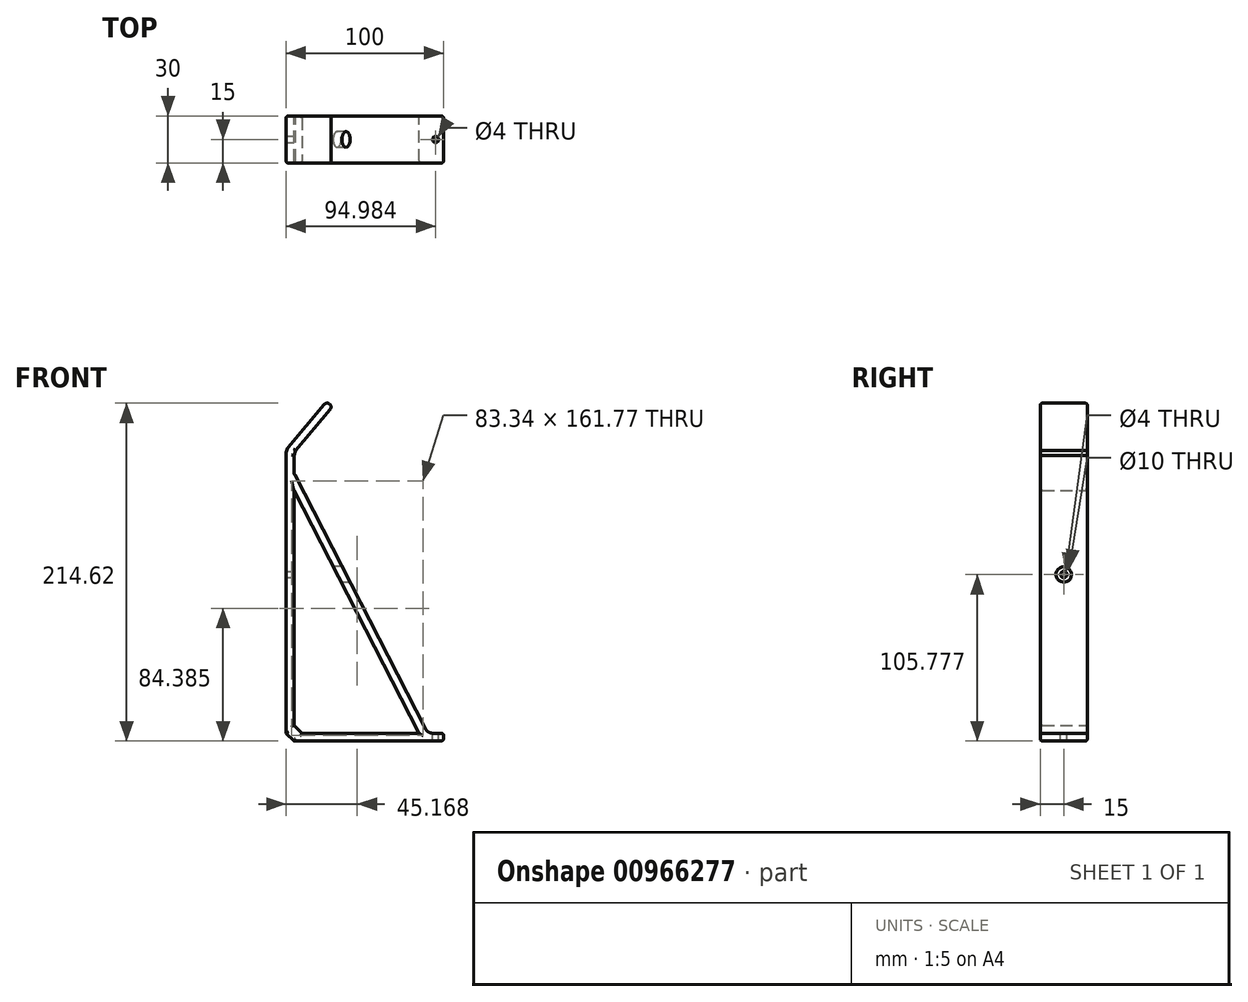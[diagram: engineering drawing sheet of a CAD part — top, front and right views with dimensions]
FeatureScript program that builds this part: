
annotation { "Feature Type Name" : "Feature", "Feature Type Description" : "" }
export const myFeature = defineFeature(function(context is Context, id is Id, definition is map)
    precondition{}
    {
        {
            var Q0;
            Q0=qCreatedBy(makeId("Front.planeOp"),FACE);
            var sketch = newSketch(context, id + "F0", { "sketchPlane" : qUnion([Q0])});
            skLineSegment(sketch, "E0", {"start": v(10, 0) * mm, "end": v(90, 0) * mm});
            skLineSegment(sketch, "E1", {"start": v(90, 0) * mm, "end": v(90, 5) * mm});
            skLineSegment(sketch, "E2", {"start": v(90, 5) * mm, "end": v(5, 5) * mm});
            skLineSegment(sketch, "E3", {"start": v(5, 5) * mm, "end": v(5, 170) * mm});
            skLineSegment(sketch, "E4", {"start": v(5, 183.18) * mm, "end": v(29.54, 212.43) * mm});
            skLineSegment(sketch, "E5", {"start": v(29.54, 212.43) * mm, "end": v(25.71, 215.64) * mm});
            skLineSegment(sketch, "E6", {"start": v(25.71, 215.64) * mm, "end": v(0, 185) * mm});
            skLineSegment(sketch, "E7", {"start": v(0, 185) * mm, "end": v(0, 5) * mm});
            skLineSegment(sketch, "E8", {"start": v(5, 170) * mm, "end": v(5, 183.18) * mm});
            skLineSegment(sketch, "E9", {"start": v(5, 170) * mm, "end": v(90, 5) * mm});
            skLineSegment(sketch, "E10", {"start": v(5, 159.08) * mm, "end": v(84.38, 5) * mm});
            skLineSegment(sketch, "E11", {"start": v(53.13, 76.58) * mm, "end": v(48.68, 74.3) * mm, "construction": true});
            skPoint(sketch, "E12.visualSharp", {"position": v(0, 0) * mm});
            skLineSegment(sketch, "E13", {"start": v(5, 5) * mm, "end": v(5, 5) * mm});
            skLineSegment(sketch, "E14", {"start": v(0, 5) * mm, "end": v(0, 0) * mm});
            skLineSegment(sketch, "E15", {"start": v(10, 0) * mm, "end": v(0, 0) * mm});
            skLineSegment(sketch, "E16", {"start": v(5, 5) * mm, "end": v(0, 5) * mm, "construction": true});
            skLineSegment(sketch, "E17.bottom", {"start": v(90, 5) * mm, "end": v(100, 5) * mm});
            skLineSegment(sketch, "E17.top", {"start": v(90, 0) * mm, "end": v(100, 0) * mm});
            skLineSegment(sketch, "E17.left", {"start": v(90, 5) * mm, "end": v(90, 0) * mm});
            skLineSegment(sketch, "E17.right", {"start": v(100, 5) * mm, "end": v(100, 0) * mm});
            skSolve(sketch);
        }
        {
            var Q0;
            Q0=makeQuery(id+"F0.imprint","IMPRINT",FACE,{"disambiguationData":[TD([[makeQuery(id+"F0.imprint","IMPRINT",EDGE,{"derivedFrom":sQuery(id+"F0.wireOp",EDGE,"E0")}),1.0]])]});
            var Q1;
            Q1=makeQuery(id+"F0.imprint","IMPRINT",FACE,{"disambiguationData":[TD([[makeQuery(id+"F0.imprint","IMPRINT",EDGE,{"derivedFrom":sQuery(id+"F0.wireOp",EDGE,"E4")}),1.0]])]});
            var Q2;
            {var subQ0=sQuery(id+"F0.wireOp",EDGE,"E9");Q2=makeQuery(id+"F0.imprint","IMPRINT",FACE,{"disambiguationData":[TD([[makeQuery(id+"F0.imprint","IMPRINT",EDGE,{"derivedFrom":subQ0}),-1.0]])]});}
            var Q3;
            Q3=makeQuery(id+"F0.imprint","IMPRINT",FACE,{"disambiguationData":[TD([[makeQuery(id+"F0.imprint","IMPRINT",EDGE,{"derivedFrom":sQuery(id+"F0.wireOp",EDGE,"E14")}),1.0]])]});
            var Q4;
            Q4=makeQuery(id+"F0.imprint","IMPRINT",FACE,{"disambiguationData":[TD([[makeQuery(id+"F0.imprint","IMPRINT",EDGE,{"derivedFrom":sQuery(id+"F0.wireOp",EDGE,"E17.bottom")}),-1.0]])]});
            extrude(context, id + "F1", {"entities" : qUnion([Q0, Q1, Q2, Q3, Q4]), "depth" : 30 * mm, "offsetDistance" : 25 * mm});
        }
        {
            var Q0;
            Q0=makeQuery(id+"F1.opExtrude","SWEPT_EDGE",EDGE,{"disambiguationData":[OSD([sQuery(id+"F0.wireOp",EDGE,"E0"),sQuery(id+"F0.wireOp",EDGE,"E1")])]});
            var Q1;
            Q1=makeQuery(id+"F1.opExtrude","SWEPT_EDGE",EDGE,{"disambiguationData":[OSD([sQuery(id+"F0.wireOp",EDGE,"E3"),sQuery(id+"F0.wireOp",EDGE,"E8"),sQuery(id+"F0.wireOp",EDGE,"E9")])]});
            fillet(context, id + "F2", {"entities" : qUnion([Q0, Q1]), "radius" : 5 * mm, "tangentPropagation" : true, "allowEdgeOverflow" : false});
        }
        {
            var Q0;
            Q0=makeQuery(id+"F1.opExtrude","SWEPT_EDGE",EDGE,{"disambiguationData":[OSD([sQuery(id+"F0.wireOp",EDGE,"E5"),sQuery(id+"F0.wireOp",EDGE,"E6")])]});
            var Q1;
            Q1=makeQuery(id+"F1.opExtrude","SWEPT_EDGE",EDGE,{"disambiguationData":[OSD([sQuery(id+"F0.wireOp",EDGE,"E4"),sQuery(id+"F0.wireOp",EDGE,"E5")])]});
            fillet(context, id + "F3", {"entities" : qUnion([Q0, Q1]), "radius" : 2.5 * mm, "tangentPropagation" : true, "allowEdgeOverflow" : false});
        }
        {
            var Q0;
            Q0=makeQuery(id+"F1.opExtrude","SWEPT_FACE",FACE,{"disambiguationData":[OSD([sQuery(id+"F0.wireOp",EDGE,"E3")])]});
            var sketch = newSketch(context, id + "F4", { "sketchPlane" : qUnion([Q0])});
            skCircle(sketch, "E18", {"center": v(-15, 105.78) * mm, "radius": 2 * mm});
            skCircle(sketch, "E19.0", {"center": v(-15, 105.78) * mm, "radius": 5 * mm});
            skLineSegment(sketch, "E20", {"start": v(-15, 105.78) * mm, "end": v(-30, 105.78) * mm, "construction": true});
            skLineSegment(sketch, "E21", {"start": v(-15, 105.78) * mm, "end": v(0, 105.78) * mm, "construction": true});
            skSolve(sketch);
        }
        {
            var Q0;
            Q0=makeQuery(id+"F4.imprint","IMPRINT",FACE,{"disambiguationData":[TD([[makeQuery(id+"F4.imprint","IMPRINT",EDGE,{"derivedFrom":sQuery(id+"F4.wireOp",EDGE,"E18")}),1.0]])]});
            extrude(context, id + "F5", {"entities" : qUnion([Q0]), "operationType" : NewBodyOperationType.REMOVE, "oppositeDirection" : true, "depth" : 25 * mm, "offsetDistance" : 25 * mm});
        }
        {
            var Q0;
            Q0=makeQuery(id+"F4.imprint","IMPRINT",FACE,{"disambiguationData":[TD([[makeQuery(id+"F4.imprint","IMPRINT",EDGE,{"derivedFrom":sQuery(id+"F4.wireOp",EDGE,"E18")}),-1.0]])]});
            var Q1;
            Q1=makeQuery(id+"F4.imprint","IMPRINT",FACE,{"disambiguationData":[TD([[makeQuery(id+"F4.imprint","IMPRINT",EDGE,{"derivedFrom":sQuery(id+"F4.wireOp",EDGE,"E18")}),1.0]])]});
            extrude(context, id + "F6", {"entities" : qUnion([Q0, Q1]), "operationType" : NewBodyOperationType.REMOVE, "depth" : 40 * mm, "offsetDistance" : 25 * mm});
        }
        {
            var Q0;
            Q0=makeQuery(id+"F1.opExtrude","SWEPT_FACE",FACE,{"disambiguationData":[OSD([sQuery(id+"F0.wireOp",EDGE,"E2")])]});
            var sketch = newSketch(context, id + "F7", { "sketchPlane" : qUnion([Q0])});
            skCircle(sketch, "E22", {"center": v(94.98, -15) * mm, "radius": 2 * mm});
            skCircle(sketch, "E23.0", {"center": v(94.98, -15) * mm, "radius": 5 * mm});
            skLineSegment(sketch, "E24", {"start": v(94.98, -15) * mm, "end": v(94.98, -30) * mm, "construction": true});
            skLineSegment(sketch, "E25", {"start": v(94.98, -15) * mm, "end": v(94.98, 0) * mm, "construction": true});
            skSolve(sketch);
        }
        {
            var Q0;
            Q0=makeQuery(id+"F7.imprint","IMPRINT",FACE,{"disambiguationData":[TD([[makeQuery(id+"F7.imprint","IMPRINT",EDGE,{"derivedFrom":sQuery(id+"F7.wireOp",EDGE,"E22")}),1.0]])]});
            extrude(context, id + "F8", {"entities" : qUnion([Q0]), "operationType" : NewBodyOperationType.REMOVE, "oppositeDirection" : true, "depth" : 25 * mm, "offsetDistance" : 25 * mm});
        }
        {
            var Q0;
            Q0=makeQuery(id+"F1.opExtrude","SWEPT_EDGE",EDGE,{"disambiguationData":[OSD([sQuery(id+"F0.wireOp",EDGE,"E2"),sQuery(id+"F0.wireOp",EDGE,"E3")])]});
            var Q1;
            Q1=makeQuery(id+"F1.opExtrude","SWEPT_EDGE",EDGE,{"disambiguationData":[OSD([sQuery(id+"F0.wireOp",EDGE,"E14"),sQuery(id+"F0.wireOp",EDGE,"E15")])]});
            var Q2;
            Q2=makeQuery(id+"F1.opExtrude","SWEPT_EDGE",EDGE,{"disambiguationData":[OSD([sQuery(id+"F0.wireOp",EDGE,"E6"),sQuery(id+"F0.wireOp",EDGE,"E7")])]});
            var Q3;
            Q3=makeQuery(id+"F1.opExtrude","SWEPT_EDGE",EDGE,{"disambiguationData":[OSD([sQuery(id+"F0.wireOp",EDGE,"E4"),sQuery(id+"F0.wireOp",EDGE,"E8")])]});
            chamfer(context, id + "F9", {"entities" : qUnion([Q0, Q1, Q2, Q3]), "width" : 5 * mm, "tangentPropagation" : true});
        }
        {
            var Q0;
            Q0=makeQuery(id+"F1.opExtrude","SWEPT_EDGE",EDGE,{"disambiguationData":[OSD([sQuery(id+"F0.wireOp",EDGE,"E17.bottom"),sQuery(id+"F0.wireOp",EDGE,"E17.right")])]});
            var Q1;
            Q1=makeQuery(id+"F1.opExtrude","CAP_FACE",FACE,{"disambiguationData":[OSD([sQuery(id+"F0.wireOp",EDGE,"E0"),sQuery(id+"F0.wireOp",EDGE,"E2"),sQuery(id+"F0.wireOp",EDGE,"E3"),sQuery(id+"F0.wireOp",EDGE,"E4"),sQuery(id+"F0.wireOp",EDGE,"E5"),sQuery(id+"F0.wireOp",EDGE,"E6"),sQuery(id+"F0.wireOp",EDGE,"E7"),sQuery(id+"F0.wireOp",EDGE,"E8"),sQuery(id+"F0.wireOp",EDGE,"E9"),sQuery(id+"F0.wireOp",EDGE,"E10"),sQuery(id+"F0.wireOp",EDGE,"E14"),sQuery(id+"F0.wireOp",EDGE,"E15"),sQuery(id+"F0.wireOp",EDGE,"E17.bottom"),sQuery(id+"F0.wireOp",EDGE,"E17.top"),sQuery(id+"F0.wireOp",EDGE,"E17.right")])],"isStart":false});
            var Q2;
            Q2=makeQuery(id+"F1.opExtrude","CAP_FACE",FACE,{"disambiguationData":[OSD([sQuery(id+"F0.wireOp",EDGE,"E0"),sQuery(id+"F0.wireOp",EDGE,"E2"),sQuery(id+"F0.wireOp",EDGE,"E3"),sQuery(id+"F0.wireOp",EDGE,"E4"),sQuery(id+"F0.wireOp",EDGE,"E5"),sQuery(id+"F0.wireOp",EDGE,"E6"),sQuery(id+"F0.wireOp",EDGE,"E7"),sQuery(id+"F0.wireOp",EDGE,"E8"),sQuery(id+"F0.wireOp",EDGE,"E9"),sQuery(id+"F0.wireOp",EDGE,"E10"),sQuery(id+"F0.wireOp",EDGE,"E14"),sQuery(id+"F0.wireOp",EDGE,"E15"),sQuery(id+"F0.wireOp",EDGE,"E17.bottom"),sQuery(id+"F0.wireOp",EDGE,"E17.top"),sQuery(id+"F0.wireOp",EDGE,"E17.right")])],"isStart":true});
            var Q3;
            Q3=makeQuery(id+"F1.opExtrude","SWEPT_EDGE",EDGE,{"disambiguationData":[OSD([sQuery(id+"F0.wireOp",EDGE,"E17.top"),sQuery(id+"F0.wireOp",EDGE,"E17.right")])]});
            var Q4;
            Q4=makeQuery(id+"F5.boolean.opBoolean","COPY",EDGE,{"derivedFrom":makeQuery(id+"F5.opExtrude","CAP_EDGE",EDGE,{"disambiguationData":[OSD([sQuery(id+"F4.wireOp",EDGE,"E18")])],"isStart":true})});
            var Q5;
            Q5=makeQuery(id+"F8.boolean.opBoolean","COPY",EDGE,{"derivedFrom":makeQuery(id+"F8.opExtrude","CAP_EDGE",EDGE,{"disambiguationData":[OSD([sQuery(id+"F7.wireOp",EDGE,"E22")])],"isStart":true})});
            var Q6;
            {var subQ0=sQuery(id+"F0.wireOp",EDGE,"E6");Q6=makeQuery(id+"F9.opChamfer","BLEND_EDGE",EDGE,{"blendedFrom":[makeQuery(id+"F1.opExtrude","SWEPT_EDGE",EDGE,{"disambiguationData":[OSD([subQ0,sQuery(id+"F0.wireOp",EDGE,"E7")])]}),makeQuery(id+"F1.opExtrude","SWEPT_FACE",FACE,{"disambiguationData":[OSD([subQ0])]})],"blendedInto":[makeQuery(id+"F1.opExtrude","SWEPT_FACE",FACE,{"disambiguationData":[OSD([subQ0])]})]});}
            var Q7;
            {var subQ0=sQuery(id+"F0.wireOp",EDGE,"E7");Q7=makeQuery(id+"F9.opChamfer","BLEND_EDGE",EDGE,{"blendedFrom":[makeQuery(id+"F1.opExtrude","SWEPT_EDGE",EDGE,{"disambiguationData":[OSD([sQuery(id+"F0.wireOp",EDGE,"E6"),subQ0])]}),makeQuery(id+"F1.opExtrude","SWEPT_FACE",FACE,{"disambiguationData":[OSD([subQ0,sQuery(id+"F0.wireOp",EDGE,"E14")])]})],"blendedInto":[makeQuery(id+"F1.opExtrude","SWEPT_FACE",FACE,{"disambiguationData":[OSD([subQ0,sQuery(id+"F0.wireOp",EDGE,"E14")])]})]});}
            fillet(context, id + "F10", {"entities" : qUnion([Q0, Q1, Q2, Q3, Q4, Q5, Q6, Q7]), "radius" : 1.5 * mm, "tangentPropagation" : true, "allowEdgeOverflow" : false});
        }
    });
